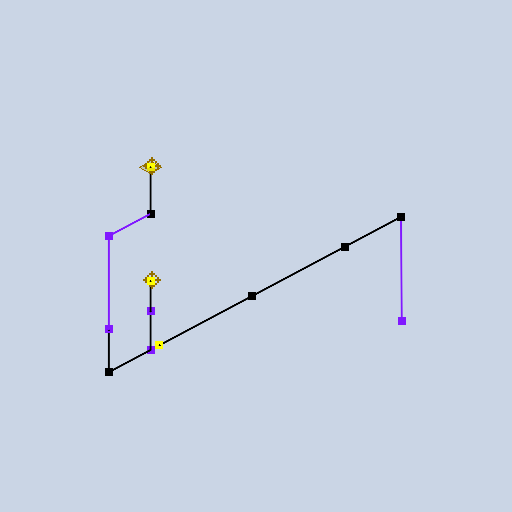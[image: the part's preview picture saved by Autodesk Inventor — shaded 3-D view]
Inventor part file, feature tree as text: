
AUTODESK INVENTOR PART (.ipt)
format: ipt  version: 2025 (Build 290162000, 162)  size: 198,144 bytes
history: native  units: in
note: dims shown in document units (in); Inventor stores cm internally (conversion verified against a paired STEP export)
features: other x10, plane x3, sketch x1
ambient origin geometry x8: Origin, YZ Plane, XZ Plane, XY Plane, X Axis, Y Axis, Z Axis, Center Point
feature tree (14):
  other  "{4D39D5F1-0985-4783-AA5A-FC16C288418C}"
  other  "Work Point3"
  plane  "Work Plane3"
  other  "Work Point4"
  other  "Work Point5"
  other  "Work Point6"
  other  "Work Point7"
  other  "Work Point8"
  other  "Work Point9"
  plane  "Work Plane4"
  other  "Work Point10"
  other  "Work Point11"
  plane  "Work Plane5"
  sketch  "3D Sketch1"
